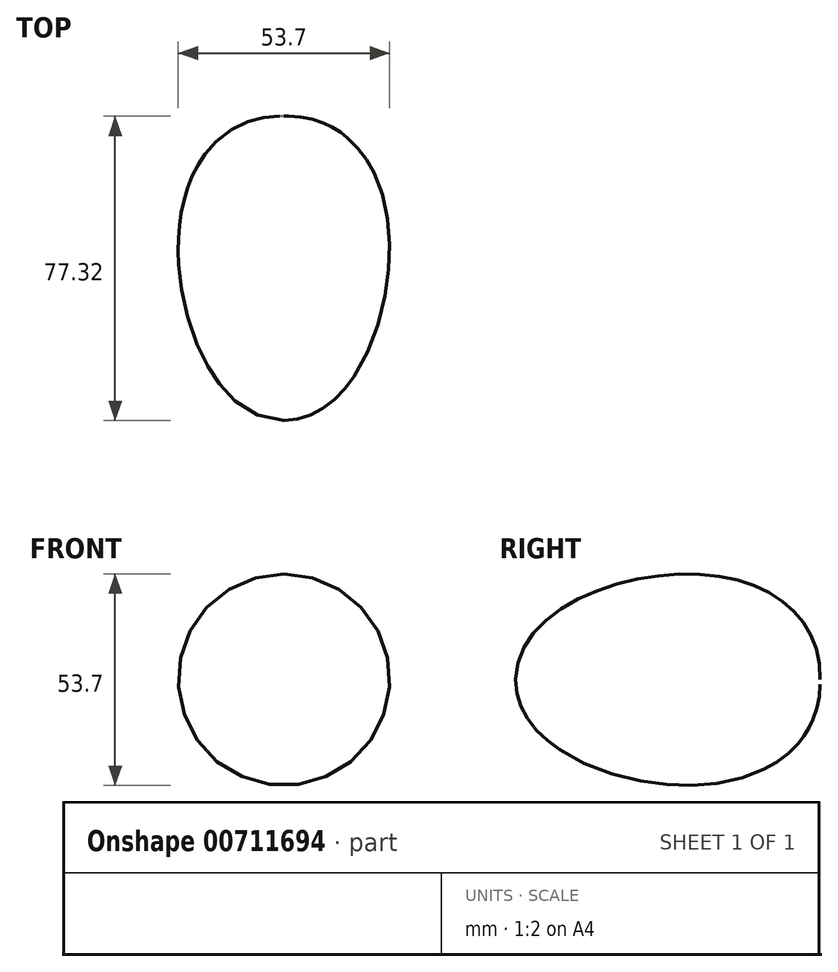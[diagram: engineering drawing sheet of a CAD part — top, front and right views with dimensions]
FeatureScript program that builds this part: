
annotation { "Feature Type Name" : "Feature", "Feature Type Description" : "" }
export const myFeature = defineFeature(function(context is Context, id is Id, definition is map)
    precondition{}
    {
        {
            var Q0;
            Q0=qCreatedBy(makeId("Right.planeOp"),FACE);
            var sketch = newSketch(context, id + "F0", { "sketchPlane" : qUnion([Q0])});
            skFitSpline(sketch, "E0", {"points": [v(-31.72, 0) * mm, v(18.33, 26.5) * mm, v(45.57, 0) * mm], "startDerivative": vector(0.65, 102.54) * mm, "endDerivative": vector(-4.18, -94.73) * mm});
            skLineSegment(sketch, "E1", {"start": v(-66.91, 0) * mm, "end": v(68.69, 0) * mm, "construction": true});
            skLineSegment(sketch, "E2", {"start": v(-31.72, 0) * mm, "end": v(45.57, 0) * mm});
            skSolve(sketch);
        }
        {
            var Q0;
            Q0 = qSketchRegion(id + "F0", true);
            var Q1;
            Q1=sQuery(id+"F0.wireOp",EDGE,"E1");
            revolve(context, id + "F1", {"surfaceOperationType" : NewSurfaceOperationType.NEW, "entities" : qUnion([Q0]), "axis" : qUnion([Q1]), "revolveType" : RevolveType.FULL});
        }
    });
